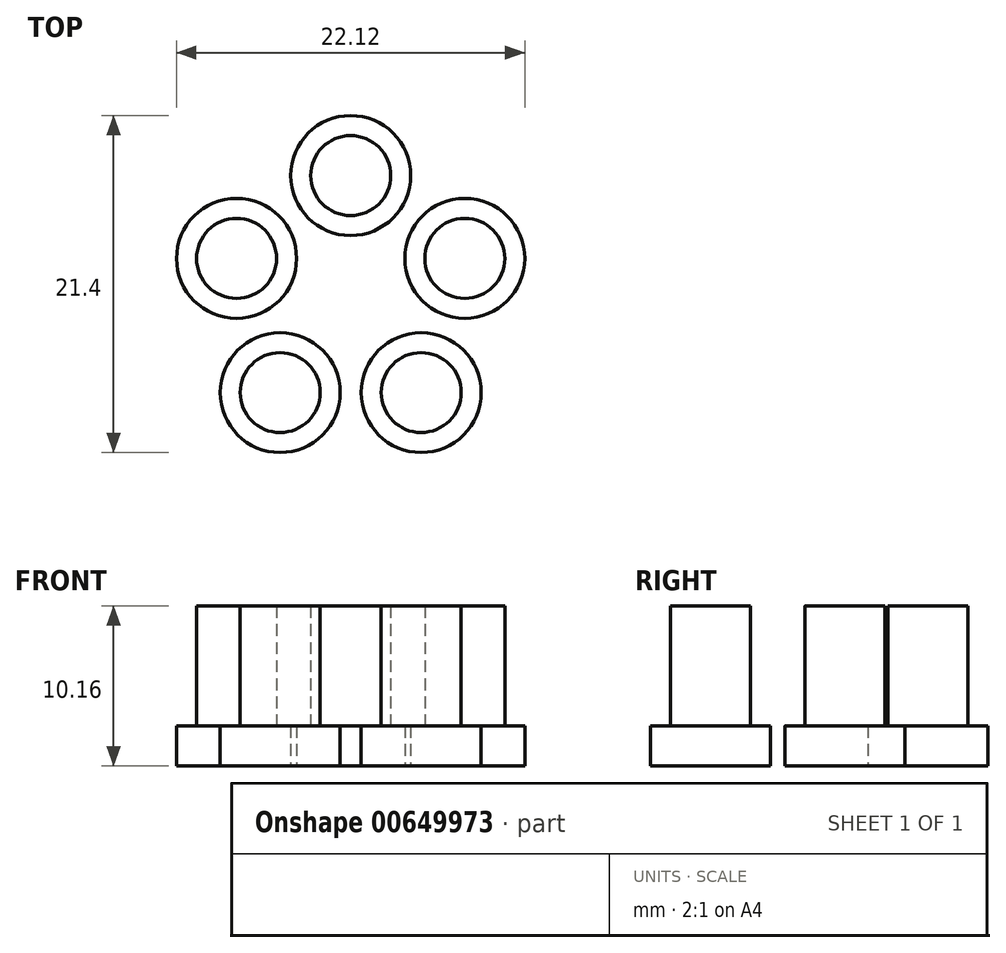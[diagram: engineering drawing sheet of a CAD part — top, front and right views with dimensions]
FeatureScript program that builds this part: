
annotation { "Feature Type Name" : "Feature", "Feature Type Description" : "" }
export const myFeature = defineFeature(function(context is Context, id is Id, definition is map)
    precondition{}
    {
        {
            var Q0;
            Q0=qCreatedBy(makeId("Top.planeOp"),FACE);
            var sketch = newSketch(context, id + "F0", { "sketchPlane" : qUnion([Q0])});
            skCircle(sketch, "E0", {"center": v(0, 0) * mm, "radius": 3.81 * mm});
            skSolve(sketch);
        }
        {
            var Q0;
            Q0 = qSketchRegion(id + "F0", true);
            extrude(context, id + "F1", {"entities" : qUnion([Q0]), "depth" : 2.54 * mm, "offsetDistance" : 25.4 * mm});
        }
        {
            var Q0;
            Q0=makeQuery(id+"F1.opExtrude","CAP_FACE",FACE,{"disambiguationData":[OSD([sQuery(id+"F0.wireOp",EDGE,"E0")])],"isStart":false});
            var sketch = newSketch(context, id + "F2", { "sketchPlane" : qUnion([Q0])});
            skCircle(sketch, "E1", {"center": v(0, 0) * mm, "radius": 2.54 * mm});
            skSolve(sketch);
        }
        {
            var Q0;
            Q0 = qSketchRegion(id + "F2", true);
            extrude(context, id + "F3", {"entities" : qUnion([Q0]), "operationType" : NewBodyOperationType.ADD, "depth" : 7.62 * mm, "offsetDistance" : 25.4 * mm});
        }
        {
            var Q0;
            Q0=qCreatedBy(makeId("Right.planeOp"),FACE);
            var sketch = newSketch(context, id + "F4", { "sketchPlane" : qUnion([Q0])});
            skLineSegment(sketch, "E2", {"start": v(-7.62, 9.42) * mm, "end": v(-7.62, -1.01) * mm});
            skSolve(sketch);
        }
        {
            var Q0;
            Q0=makeQuery(id+"F1.opExtrude","SWEPT_BODY",BODY,{"disambiguationData":[OSD([sQuery(id+"F0.wireOp",EDGE,"E0")])]});
            var Q1;
            Q1=sQuery(id+"F4.wireOp",EDGE,"E2");
            circularPattern(context, id + "F5", {"entities" : qUnion([Q0]), "axis" : qUnion([Q1]), "angle" : 360 * degree, "instanceCount" : 5, "equalSpace" : true});
        }
    });
